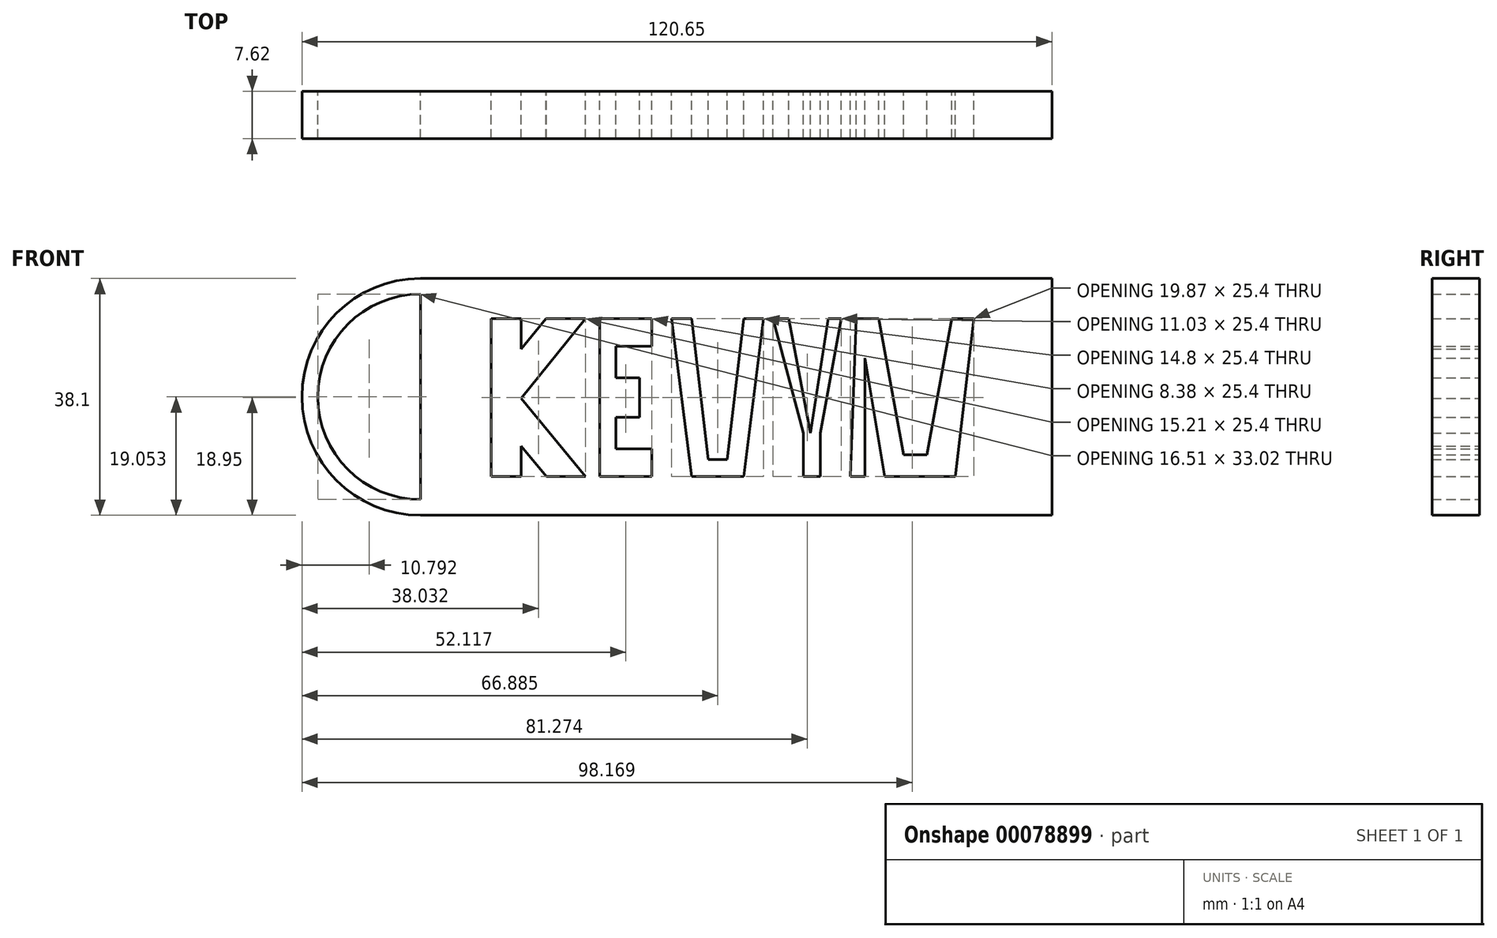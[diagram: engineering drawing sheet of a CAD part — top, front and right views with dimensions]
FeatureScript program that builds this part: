
annotation { "Feature Type Name" : "Feature", "Feature Type Description" : "" }
export const myFeature = defineFeature(function(context is Context, id is Id, definition is map)
    precondition{}
    {
        {
            var Q0;
            Q0=qCreatedBy(makeId("Front.planeOp"),FACE);
            var sketch = newSketch(context, id + "F0", { "sketchPlane" : qUnion([Q0])});
            skLineSegment(sketch, "E0.bottom", {"start": v(0, -1.3) * mm, "end": v(-87.51, -1.3) * mm});
            skLineSegment(sketch, "E0.top", {"start": v(-6.76, 24.1) * mm, "end": v(-10.34, 24.1) * mm});
            skLineSegment(sketch, "E0.left", {"start": v(0, -1.3) * mm, "end": v(0, 24.1) * mm});
            skLineSegment(sketch, "E0.right", {"start": v(-87.51, -1.3) * mm, "end": v(-87.51, 24.1) * mm});
            skLineSegment(sketch, "E1", {"start": v(-84.44, 24.1) * mm, "end": v(-84.44, -1.3) * mm});
            skLineSegment(sketch, "E2", {"start": v(-84.44, -1.3) * mm, "end": v(-79.58, -1.3) * mm});
            skLineSegment(sketch, "E3", {"start": v(-79.58, -1.3) * mm, "end": v(-79.58, 3.56) * mm});
            skLineSegment(sketch, "E4", {"start": v(-79.58, 3.56) * mm, "end": v(-75.56, -1.3) * mm});
            skLineSegment(sketch, "E5", {"start": v(-84.44, 24.1) * mm, "end": v(-79.58, 24.1) * mm});
            skPoint(sketch, "E5.endSnap0", {"position": v(-79.58, 1.12) * mm});
            skLineSegment(sketch, "E6", {"start": v(-79.58, 24.1) * mm, "end": v(-79.58, 19.17) * mm});
            skLineSegment(sketch, "E7", {"start": v(-79.58, 19.17) * mm, "end": v(-75.62, 24.1) * mm});
            skLineSegment(sketch, "E8", {"start": v(-75.62, 24.1) * mm, "end": v(-69.22, 24.1) * mm});
            skLineSegment(sketch, "E9", {"start": v(-69.22, 24.1) * mm, "end": v(-79.58, 11.24) * mm});
            skLineSegment(sketch, "E10", {"start": v(-79.58, 11.24) * mm, "end": v(-69.22, -1.3) * mm});
            skLineSegment(sketch, "E11", {"start": v(-69.22, -1.3) * mm, "end": v(-75.56, -1.3) * mm});
            skLineSegment(sketch, "E12", {"start": v(-58.55, 24.1) * mm, "end": v(-66.93, 24.1) * mm});
            skLineSegment(sketch, "E13", {"start": v(-66.93, 24.1) * mm, "end": v(-66.93, -1.3) * mm});
            skLineSegment(sketch, "E14", {"start": v(-66.93, -1.3) * mm, "end": v(-58.55, -1.3) * mm});
            skLineSegment(sketch, "E15", {"start": v(-58.55, -1.3) * mm, "end": v(-58.55, 3.14) * mm});
            skLineSegment(sketch, "E16", {"start": v(-58.55, 3.14) * mm, "end": v(-64.33, 3.14) * mm});
            skLineSegment(sketch, "E17", {"start": v(-64.33, 3.14) * mm, "end": v(-64.33, 8.22) * mm});
            skLineSegment(sketch, "E18", {"start": v(-64.33, 8.22) * mm, "end": v(-60.52, 8.22) * mm});
            skLineSegment(sketch, "E19", {"start": v(-60.52, 8.22) * mm, "end": v(-60.52, 14.57) * mm});
            skLineSegment(sketch, "E20", {"start": v(-60.52, 14.57) * mm, "end": v(-64.33, 14.57) * mm});
            skLineSegment(sketch, "E21", {"start": v(-64.33, 14.57) * mm, "end": v(-64.33, 19.65) * mm});
            skLineSegment(sketch, "E22", {"start": v(-64.33, 19.65) * mm, "end": v(-58.55, 19.65) * mm});
            skLineSegment(sketch, "E23", {"start": v(-58.55, 19.65) * mm, "end": v(-58.55, 24.1) * mm});
            skLineSegment(sketch, "E24", {"start": v(-55.37, 24.1) * mm, "end": v(-52.2, -1.3) * mm});
            skLineSegment(sketch, "E25", {"start": v(-52.2, -1.3) * mm, "end": v(-43.76, -1.3) * mm});
            skLineSegment(sketch, "E26", {"start": v(-43.76, -1.3) * mm, "end": v(-40.58, 24.1) * mm});
            skLineSegment(sketch, "E27", {"start": v(-40.58, 24.1) * mm, "end": v(-43.76, 24.1) * mm});
            skLineSegment(sketch, "E28", {"start": v(-43.76, 24.1) * mm, "end": v(-46.43, 1.39) * mm});
            skLineSegment(sketch, "E29", {"start": v(-52.2, 24.1) * mm, "end": v(-55.37, 24.1) * mm});
            skLineSegment(sketch, "E30", {"start": v(-46.43, 1.39) * mm, "end": v(-49.53, 1.39) * mm});
            skLineSegment(sketch, "E31", {"start": v(-52.2, 24.1) * mm, "end": v(-49.53, 1.39) * mm});
            skLineSegment(sketch, "E32", {"start": v(-34.22, -1.3) * mm, "end": v(-31.48, -1.3) * mm});
            skPoint(sketch, "E33.endSnap0", {"position": v(-35.58, 11.45) * mm});
            skLineSegment(sketch, "E34", {"start": v(-28.07, 24.1) * mm, "end": v(-30.22, 24.1) * mm});
            skLineSegment(sketch, "E35", {"start": v(-36.56, 24.1) * mm, "end": v(-39.1, 24.1) * mm});
            skLineSegment(sketch, "E36", {"start": v(-26.62, -1.3) * mm, "end": v(-25.65, 24.1) * mm});
            skLineSegment(sketch, "E37", {"start": v(-25.65, 24.1) * mm, "end": v(-22.07, 24.1) * mm});
            skLineSegment(sketch, "E38", {"start": v(-22.07, 24.1) * mm, "end": v(-18.07, 2.18) * mm});
            skLineSegment(sketch, "E39", {"start": v(-18.07, 2.18) * mm, "end": v(-14.35, 2.18) * mm});
            skLineSegment(sketch, "E40", {"start": v(-14.35, 2.18) * mm, "end": v(-10.34, 24.1) * mm});
            skLineSegment(sketch, "E41", {"start": v(-10.34, 24.1) * mm, "end": v(-6.76, 24.1) * mm});
            skLineSegment(sketch, "E42", {"start": v(-6.76, 24.1) * mm, "end": v(-9.76, -1.3) * mm});
            skLineSegment(sketch, "E43", {"start": v(-9.76, -1.3) * mm, "end": v(-21.1, -1.3) * mm});
            skLineSegment(sketch, "E44", {"start": v(-26.62, -1.3) * mm, "end": v(-24.3, -1.3) * mm});
            skLineSegment(sketch, "E45", {"start": v(-24.3, -1.3) * mm, "end": v(-24.3, 17.75) * mm});
            skLineSegment(sketch, "E46", {"start": v(-24.3, 17.75) * mm, "end": v(-21.1, -1.3) * mm});
            skLineSegment(sketch, "E47", {"start": v(-39.1, 24.1) * mm, "end": v(-36.56, 24.1) * mm});
            skLineSegment(sketch, "E48.trimOffspring", {"start": v(-40.58, 24.1) * mm, "end": v(-87.51, 24.1) * mm});
            skLineSegment(sketch, "E49", {"start": v(-40.58, 24.1) * mm, "end": v(-39.1, 24.1) * mm});
            skLineSegment(sketch, "E50", {"start": v(-36.56, 24.1) * mm, "end": v(-30.22, 24.1) * mm});
            skLineSegment(sketch, "E51", {"start": v(-34.22, -1.3) * mm, "end": v(-34.22, 5.68) * mm});
            skLineSegment(sketch, "E52", {"start": v(-34.22, 5.68) * mm, "end": v(-39.1, 24.1) * mm});
            skLineSegment(sketch, "E53", {"start": v(-31.48, -1.3) * mm, "end": v(-31.48, 5.68) * mm});
            skLineSegment(sketch, "E54", {"start": v(-31.48, 5.68) * mm, "end": v(-28.07, 24.1) * mm});
            skLineSegment(sketch, "E55", {"start": v(-36.56, 24.1) * mm, "end": v(-33.03, 5.68) * mm});
            skLineSegment(sketch, "E56", {"start": v(-33.03, 5.68) * mm, "end": v(-30.22, 24.1) * mm});
            skLineSegment(sketch, "E57.trimOffspring", {"start": v(-22.07, 24.1) * mm, "end": v(-25.65, 24.1) * mm});
            skLineSegment(sketch, "E58", {"start": v(-28.07, 24.1) * mm, "end": v(-25.65, 24.1) * mm});
            skLineSegment(sketch, "E59", {"start": v(-22.07, 24.1) * mm, "end": v(-10.34, 24.1) * mm});
            skLineSegment(sketch, "E60", {"start": v(-6.76, 24.1) * mm, "end": v(0, 24.1) * mm});
            skLineSegment(sketch, "E61.bottom", {"start": v(5.79, -7.56) * mm, "end": v(-95.81, -7.56) * mm});
            skLineSegment(sketch, "E61.top", {"start": v(5.79, 30.54) * mm, "end": v(-95.81, 30.54) * mm});
            skLineSegment(sketch, "E61.left", {"start": v(5.79, -7.56) * mm, "end": v(5.79, 30.54) * mm});
            skLineSegment(sketch, "E61.right", {"start": v(-95.81, -7.56) * mm, "end": v(-95.81, 30.54) * mm});
            skArc(sketch, "E62", {"start": v(-95.81, 30.54) * mm, "mid": v(-114.86, 11.5) * mm, "end": v(-95.81, -7.56) * mm});
            skArc(sketch, "E63", {"start": v(-95.81, 28) * mm, "mid": v(-112.32, 11.5) * mm, "end": v(-95.81, -5.02) * mm});
            skSolve(sketch);
        }
        {
            var Q0;
            {var subQ21=sQuery(id+"F0.wireOp",EDGE,"E0.left");Q0=makeQuery(id+"F0.imprint","IMPRINT",FACE,{"disambiguationData":[TD([[makeQuery(id+"F0.imprint","IMPRINT",EDGE,{"derivedFrom":subQ21}),-1.0]])]});}
            var Q1;
            {var subQ0=sQuery(id+"F0.wireOp",EDGE,"E0.left");Q1=makeQuery(id+"F0.imprint","IMPRINT",FACE,{"disambiguationData":[TD([[makeQuery(id+"F0.imprint","IMPRINT",EDGE,{"derivedFrom":subQ0}),1.0]])]});}
            var Q2;
            Q2=makeQuery(id+"F0.imprint","IMPRINT",FACE,{"disambiguationData":[TD([[makeQuery(id+"F0.imprint","IMPRINT",EDGE,{"derivedFrom":sQuery(id+"F0.wireOp",EDGE,"E38")}),1.0]])]});
            var Q3;
            {var subQ2=sQuery(id+"F0.wireOp",EDGE,"E45");Q3=makeQuery(id+"F0.imprint","IMPRINT",FACE,{"disambiguationData":[TD([[makeQuery(id+"F0.imprint","IMPRINT",EDGE,{"derivedFrom":subQ2}),-1.0]])]});}
            var Q4;
            {var subQ0=sQuery(id+"F0.wireOp",EDGE,"E36");Q4=makeQuery(id+"F0.imprint","IMPRINT",FACE,{"disambiguationData":[TD([[makeQuery(id+"F0.imprint","IMPRINT",EDGE,{"derivedFrom":subQ0}),1.0]])]});}
            var Q5;
            {var subQ1=sQuery(id+"F0.wireOp",EDGE,"E26");Q5=makeQuery(id+"F0.imprint","IMPRINT",FACE,{"disambiguationData":[TD([[makeQuery(id+"F0.imprint","IMPRINT",EDGE,{"derivedFrom":subQ1}),-1.0]])]});}
            var Q6;
            Q6=makeQuery(id+"F0.imprint","IMPRINT",FACE,{"disambiguationData":[TD([[makeQuery(id+"F0.imprint","IMPRINT",EDGE,{"derivedFrom":sQuery(id+"F0.wireOp",EDGE,"E50")}),-1.0]])]});
            var Q7;
            {var subQ0=sQuery(id+"F0.wireOp",EDGE,"E28");Q7=makeQuery(id+"F0.imprint","IMPRINT",FACE,{"disambiguationData":[TD([[makeQuery(id+"F0.imprint","IMPRINT",EDGE,{"derivedFrom":subQ0}),-1.0]])]});}
            var Q8;
            {var subQ3=sQuery(id+"F0.wireOp",EDGE,"E15");Q8=makeQuery(id+"F0.imprint","IMPRINT",FACE,{"disambiguationData":[TD([[makeQuery(id+"F0.imprint","IMPRINT",EDGE,{"derivedFrom":subQ3}),-1.0]])]});}
            var Q9;
            {var subQ1=sQuery(id+"F0.wireOp",EDGE,"E9");Q9=makeQuery(id+"F0.imprint","IMPRINT",FACE,{"disambiguationData":[TD([[makeQuery(id+"F0.imprint","IMPRINT",EDGE,{"derivedFrom":subQ1}),1.0]])]});}
            var Q10;
            {var subQ0=sQuery(id+"F0.wireOp",EDGE,"E0.right");Q10=makeQuery(id+"F0.imprint","IMPRINT",FACE,{"disambiguationData":[TD([[makeQuery(id+"F0.imprint","IMPRINT",EDGE,{"derivedFrom":subQ0}),-1.0]])]});}
            var Q11;
            {var subQ0=sQuery(id+"F0.wireOp",EDGE,"E6");Q11=makeQuery(id+"F0.imprint","IMPRINT",FACE,{"disambiguationData":[TD([[makeQuery(id+"F0.imprint","IMPRINT",EDGE,{"derivedFrom":subQ0}),1.0]])]});}
            var Q12;
            {var subQ0=sQuery(id+"F0.wireOp",EDGE,"E3");Q12=makeQuery(id+"F0.imprint","IMPRINT",FACE,{"disambiguationData":[TD([[makeQuery(id+"F0.imprint","IMPRINT",EDGE,{"derivedFrom":subQ0}),-1.0]])]});}
            var Q13;
            {var subQ0=sQuery(id+"F0.wireOp",EDGE,"E62");Q13=makeQuery(id+"F0.imprint","IMPRINT",FACE,{"disambiguationData":[TD([[makeQuery(id+"F0.imprint","IMPRINT",EDGE,{"derivedFrom":subQ0}),1.0]])]});}
            extrude(context, id + "F1", {"entities" : qUnion([Q0, Q1, Q2, Q3, Q4, Q5, Q6, Q7, Q8, Q9, Q10, Q11, Q12, Q13]), "depth" : 7.62 * mm});
        }
    });
